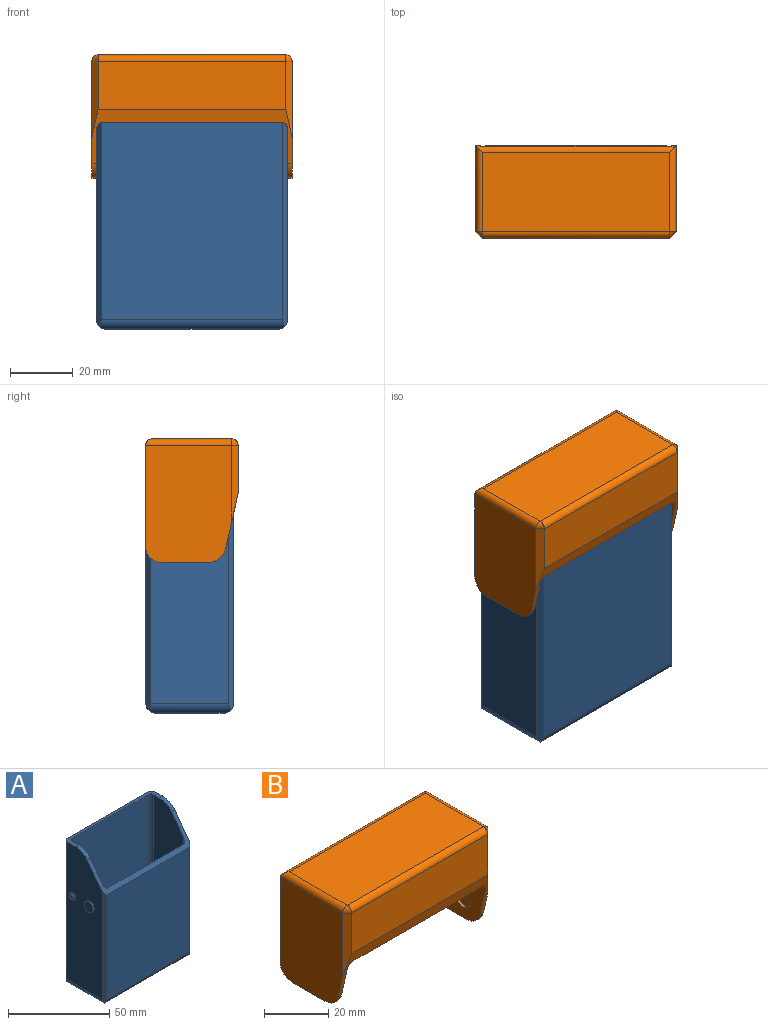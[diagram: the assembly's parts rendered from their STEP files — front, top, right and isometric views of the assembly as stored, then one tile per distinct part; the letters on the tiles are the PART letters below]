
ASSEMBLY  parts=2 mates=1
PART A: 34 faces, bbox 63x28x86.2 mm
  f0: plane 61x8mm, normal (0,0,1), area 130.9mm2, adj f2,f3,f5,f7,f8,f11,f12,f13
  f1: plane 61x16mm, normal (0,-0.8,0.6), area 247.5mm2, adj f3,f4,f5,f7,f8,f10,f12,f13
  f2: plane 83.2x58mm, normal (0,1,0), area 4825.6mm2, adj f0,f18,f19,f23
  f3: plane 83.2x25mm, normal (-1,0,0), area 1914mm2, adj f0,f1,f13,f19,f20,f25,f28,f32
  f4: plane 63.2x58mm, normal (0,-1,0), area 3665.6mm2, adj f1,f20,f21,f24
  f5: plane 83.2x25mm, normal (1,0,0), area 1914mm2, adj f0,f1,f12,f18,f21,f22,f26,f33
  f6: plane 55x22mm, normal (0,0,-1), area 1210mm2, adj f22,f23,f24,f25
  f7: plane 84x20.6mm, normal (1,0,0), area 1641.6mm2, adj f0,f1,f9,f13,f15,f16
  f8: plane 84x20.6mm, normal (-1,0,0), area 1641.6mm2, adj f0,f1,f9,f12,f14,f17
  f9: plane 56.6x24.6mm, normal (0,0,1), area 1388.9mm2, adj f7,f8,f10,f11,f14,f15,f16,f17
  f10: plane 66.27x52.6mm, normal (0,1,0), area 3485.6mm2, adj f1,f9,f16,f17
  f11: plane 84x52.6mm, normal (0,-1,0), area 4418.4mm2, adj f0,f9,f14,f15
  f12: cylinder r=10mm len=8mm, axis (1,0,0), area 20.4mm2, adj f0,f1,f5,f8
  f13: cylinder r=10mm len=8mm, axis (1,0,0), area 20.4mm2, adj f0,f1,f3,f7
  f14: cylinder r=2mm len=84mm, axis (0,0,1), area 263.9mm2, adj f0,f8,f9,f11
  f15: cylinder r=2mm len=84mm, axis (0,0,-1), area 263.9mm2, adj f0,f7,f9,f11
  f16: cylinder r=2mm len=68.93mm, axis (0,0,1), area 211.2mm2, adj f1,f7,f9,f10
  f17: cylinder r=2mm len=68.93mm, axis (0,0,-1), area 211.2mm2, adj f1,f8,f9,f10
  f18: plane 85.18x1.5mm, normal (0.71,0.71,0), area 179.4mm2, adj f0,f2,f5,f22,f23
  f19: plane 85.18x1.5mm, normal (-0.71,0.71,0), area 179.4mm2, adj f0,f2,f3,f23,f25
  f20: plane 67.18x1.5mm, normal (-0.71,-0.71,0), area 139.1mm2, adj f1,f3,f4,f24,f25
  f21: plane 67.18x1.5mm, normal (0.71,-0.71,0), area 139.1mm2, adj f1,f4,f5,f22,f24
  f22: cylinder r=3mm len=26.5mm, axis (0,1,0), area 117.4mm2, adj f5,f6,f18,f21,f23,f24
  f23: cylinder r=3mm len=59.5mm, axis (-1,0,0), area 272.9mm2, adj f2,f6,f18,f19,f22,f25
  f24: cylinder r=3mm len=59.5mm, axis (1,0,0), area 272.9mm2, adj f4,f6,f20,f21,f22,f25
  f25: cylinder r=3mm len=26.5mm, axis (0,-1,0), area 117.4mm2, adj f3,f6,f19,f20,f23,f24
  f26: cylinder r=3mm len=6mm, axis (-1,0,0), area 18.8mm2, adj f5,f27
  f27: plane 6x6mm, normal (1,0,0), area 28.3mm2, adj f26
  f28: cylinder r=3mm len=6mm, axis (1,0,0), area 18.8mm2, adj f3,f29
  f29: plane 6x6mm, normal (-1,0,0), area 28.3mm2, adj f28
  f30: plane 2x2mm, normal (1,0,0), area 3.1mm2, adj f33
  f31: plane 2x2mm, normal (-1,0,0), area 3.1mm2, adj f32
  f32: torus R=1mm, axis (-1,0,0), area 16.2mm2, adj f3,f31
  f33: torus R=1mm, axis (1,0,0), area 16.2mm2, adj f5,f30
PART B: 46 faces, bbox 65.2x33.2x42.2 mm
  f0: plane 32.5x1.5mm, normal (0,1,0), area 48.8mm2, adj f6,f12,f16,f17
  f1: plane 15.93x2.71mm, normal (0,0,-1), area 17.5mm2, adj f5,f8,f15,f23,f39,f40
  f2: plane 60x15.5mm, normal (0,-1,0), area 930mm2, adj f20,f21,f24,f26
  f3: plane 32.5x1.5mm, normal (0,1,0), area 48.7mm2, adj f5,f8,f15,f17
  f4: plane 15.92x2.71mm, normal (0,0,-1), area 17.5mm2, adj f6,f12,f16,f22,f41,f43
  f5: plane 37.5x27.5mm, normal (1,0,0), area 1001.6mm2, adj f1,f3,f15,f19,f21,f23,f26
  f6: plane 37.5x27.5mm, normal (-1,0,0), area 1001.6mm2, adj f0,f4,f16,f18,f21,f22,f24
  f7: plane 60x25.5mm, normal (0,0,1), area 1530mm2, adj f17,f18,f19,f20
  f8: plane 38.2x28.13mm, normal (-1,0,0), area 914.2mm2, adj f1,f3,f9,f13,f15,f17,f21,f23
  f9: plane 22.24x2mm, normal (-0.71,0.71,0), area 58.5mm2, adj f8,f10,f13,f29
  f10: plane 57x20.24mm, normal (0,1,0), area 1153.9mm2, adj f9,f11,f13,f14
  f11: plane 22.24x2mm, normal (0.71,0.71,0), area 58.5mm2, adj f10,f12,f13,f28
  f12: plane 38.2x28.13mm, normal (1,0,0), area 914.2mm2, adj f0,f4,f11,f13,f16,f17,f21,f22
  f13: plane 61x27.64mm, normal (0,0,-1), area 1682.2mm2, adj f8,f9,f10,f11,f12,f17
  f14: plane 57x0.81mm, normal (0,0,-1), area 46.2mm2, adj f10,f21,f28,f29
  f15: cylinder r=5mm len=5mm, axis (-1,0,0), area 11.8mm2, adj f1,f3,f5,f8,f45
  f16: cylinder r=5mm len=5mm, axis (-1,0,0), area 11.8mm2, adj f0,f4,f6,f12,f44
  f17: cylinder r=2mm len=64mm, axis (1,0,0), area 152.9mm2, adj f0,f3,f7,f8,f12,f13,f18,f19
  f18: cylinder r=2mm len=27.5mm, axis (0,1,0), area 83.3mm2, adj f6,f7,f17,f25
  f19: cylinder r=2mm len=27.5mm, axis (0,-1,0), area 83.3mm2, adj f5,f7,f17,f27
  f20: cylinder r=2mm len=60mm, axis (-1,0,0), area 188.5mm2, adj f2,f7,f25,f27
  f21: plane 64.19x17.52mm, normal (0,-0.98,-0.22), area 290mm2, adj f2,f5,f6,f8,f12,f14,f22,f23
  f22: cylinder r=6mm len=5.85mm, axis (-1,0,0), area 12.1mm2, adj f4,f6,f12,f21
  f23: cylinder r=6mm len=5.85mm, axis (-1,0,0), area 12.1mm2, adj f1,f5,f8,f21
  f24: plane 24.3x2mm, normal (-0.71,-0.71,0), area 56.3mm2, adj f2,f6,f21,f25
  f25: bspline ~2x2mm, area 3mm2, adj f18,f20,f24
  f26: plane 24.3x2mm, normal (0.71,-0.71,0), area 56.3mm2, adj f2,f5,f21,f27
  f27: bspline ~2x2mm, area 3mm2, adj f19,f20,f26
  f28: cylinder r=2mm len=2.81mm, axis (0,1,0), area 5.8mm2, adj f11,f12,f14,f21
  f29: cylinder r=2mm len=2.81mm, axis (0,-1,0), area 5.8mm2, adj f8,f9,f14,f21
  f30: cylinder r=3.2mm len=6.4mm, axis (-1,0,0), area 20.1mm2, adj f8,f31
  f31: plane 6.4x6.4mm, normal (-1,0,0), area 32.2mm2, adj f30
  f32: cylinder r=3.2mm len=6.4mm, axis (1,0,0), area 20.1mm2, adj f12,f33
  f33: plane 6.4x6.4mm, normal (1,0,0), area 32.2mm2, adj f32
  f34: plane 2x2mm, normal (-1,0,0), area 3.1mm2, adj f35
  f35: torus R=1mm, axis (-1,0,0), area 16.2mm2, adj f8,f34,f40
  f36: plane 2x2mm, normal (1,0,0), area 3.1mm2, adj f37
  f37: torus R=1mm, axis (1,0,0), area 16.2mm2, adj f12,f36,f43
  f38: cylinder r=14mm len=5.03mm, axis (-1,0,0), area 1.2mm2, adj f8,f40,f45
  f39: cylinder r=10mm len=7mm, axis (-1,0,0), area 3.6mm2, adj f1,f8,f40
  f40: cone r=2mm half-angle=81.9deg, axis (1,0,0), area 26.9mm2, adj f1,f35,f38,f39,f45
  f41: cylinder r=10mm len=7mm, axis (1,0,0), area 3.6mm2, adj f4,f12,f43
  f42: cylinder r=14mm len=5.03mm, axis (1,0,0), area 1.2mm2, adj f12,f43,f44
  f43: cone r=2mm half-angle=81.9deg, axis (-1,0,0), area 26.9mm2, adj f4,f37,f41,f42,f44
  f44: cylinder r=3mm len=1.97mm, axis (1,0,0), area 1.2mm2, adj f12,f16,f42,f43
  f45: cylinder r=3mm len=1.97mm, axis (-1,0,0), area 1.2mm2, adj f8,f15,f38,f40
PLACE A t=(-38.96,0.21,-4.74)mm fixed
PLACE B rot(axis=(1,0,0),0deg) t=(-38.96,0.21,61.46)mm
MATE revolute A.f26 <-> B.f30  axis (1,0,0) through (-7.46,-3.79,50.46)mm
